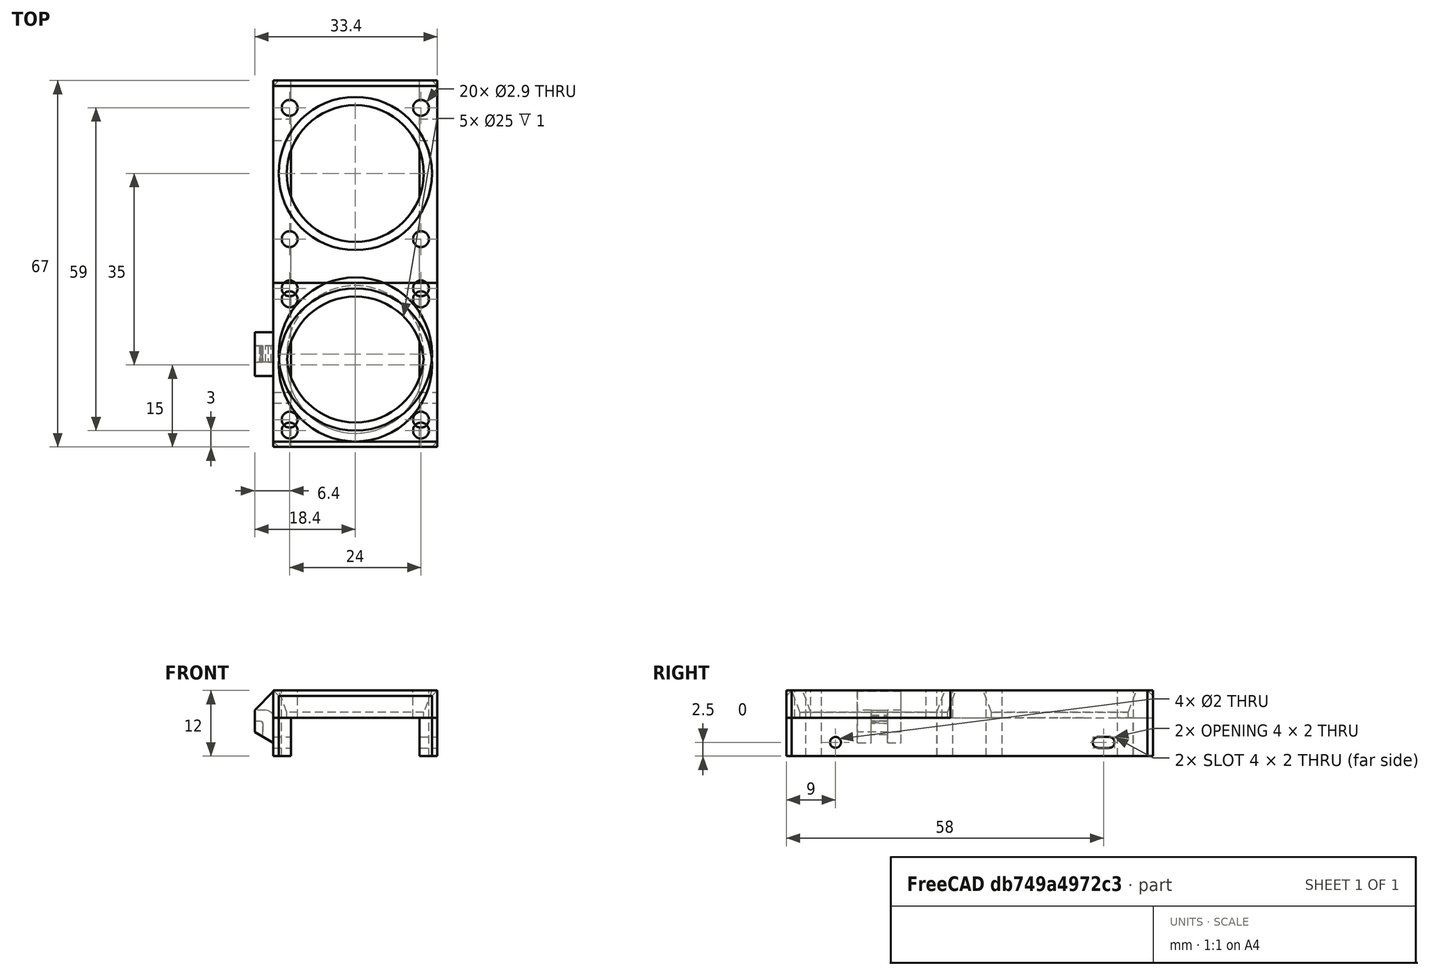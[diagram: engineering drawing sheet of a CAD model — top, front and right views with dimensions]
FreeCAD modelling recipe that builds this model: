
FCSTD DOCUMENT  (FreeCAD 0.18R16146 (Git))
Label: nvme-cooler-mount
License: All rights reserved
LicenseURL: http://en.wikipedia.org/wiki/All_rights_reserved
objects: Part::Cylinder×11, Part::Box×7, Part::MultiFuse×7, Part::Feature×6, Part::Cut×4, Part::Chamfer×2
note: 37 computed .brp shape members not serialized (recipe doc carries the construction recipe); baked Part::Feature solids carry a one-line shape summary decoded from their .brp

FEATURE [Part::Box] Box  label="Cube"
  AttacherType = Attacher::AttachEngine3D
  Height = 5
  Length = 30
  Placement = pos=(-15,-15,0) rot=(0,0,1;0rad)
  Width = 30
FEATURE [Part::Cylinder] Cylinder
  Angle = 360
  AttacherType = Attacher::AttachEngine3D
  Height = 10
  Placement = pos=(12,12,0) rot=(0,0,1;0rad)
  Radius = 1.45
FEATURE [Part::Cylinder] Cylinder001
  Angle = 360
  AttacherType = Attacher::AttachEngine3D
  Height = 10
  Placement = pos=(-12,12,0) rot=(0,0,1;0rad)
  Radius = 1.45
FEATURE [Part::Cylinder] Cylinder002
  Angle = 360
  AttacherType = Attacher::AttachEngine3D
  Height = 10
  Placement = pos=(12,-12,0) rot=(0,0,1;0rad)
  Radius = 1.45
FEATURE [Part::Cylinder] Cylinder003
  Angle = 360
  AttacherType = Attacher::AttachEngine3D
  Height = 10
  Placement = pos=(-12,-12,0) rot=(0,0,1;0rad)
  Radius = 1.45
FEATURE [Part::Cylinder] Cylinder004
  Angle = 360
  AttacherType = Attacher::AttachEngine3D
  Height = 10
  Radius = 12.5
FEATURE [Part::MultiFuse] Fusion
  Shapes = -> [Cylinder003,Cylinder001,Cylinder,Cylinder002]
FEATURE [Part::Cut] Cut
  Base = -> Box
  Tool = -> Fusion
FEATURE [Part::Cut] Cut001
  Base = -> Cut
  Tool = -> Cylinder004
FEATURE [Part::Chamfer] Chamfer  label="fan-template"
  Base = -> Cut001
  Edges = 1 edges: [Edge11 r1=1.5 r2=4]
FEATURE [Part::Feature] Chamfer001  label="fan-template001"
  Placement = pos=(0,2,0) rot=(0,0,1;0rad)
  shape: bbox 30 x 30 x 5 mm, 12 faces (baked)
FEATURE [Part::Feature] Chamfer002  label="fan-template002"
  Placement = pos=(0,35,0) rot=(0,0,1;0rad)
  shape: bbox 30 x 30 x 5 mm, 12 faces (baked)
FEATURE [Part::Box] Box001  label="Cube001"
  AttacherType = Attacher::AttachEngine3D
  Height = 5
  Length = 30
  Placement = pos=(-15,17,0) rot=(0,0,1;0rad)
  Width = 3
FEATURE [Part::Box] Box002  label="Cube002"
  AttacherType = Attacher::AttachEngine3D
  Height = 5
  Length = 30
  Placement = pos=(-15,-15,0) rot=(0,0,1;0rad)
  Width = 2
FEATURE [Part::Box] Box003  label="Cube003"
  AttacherType = Attacher::AttachEngine3D
  Height = 7
  Length = 3.25
  Placement = pos=(-15,-15,-7) rot=(0,0,1;0rad)
  Width = 67
FEATURE [Part::Box] Box004  label="Cube004"
  AttacherType = Attacher::AttachEngine3D
  Height = 7
  Length = 3.25
  Placement = pos=(11.75,-15,-7) rot=(0,0,1;0rad)
  Width = 67
FEATURE [Part::Box] Box005  label="Cube005"
  AttacherType = Attacher::AttachEngine3D
  Height = 5
  Length = 30
  Placement = pos=(-15,50,0) rot=(0,0,1;0rad)
  Width = 2
FEATURE [Part::Feature] Part__Feature001  label="Common003"
  Placement = pos=(-77.65,-16.5,25.4) rot=(0.707107,0.707107,0;3.14159rad)
  shape: bbox 3.5 x 8 x 9.5 mm, 30 faces (baked)
FEATURE [Part::Cylinder] Cylinder006
  Angle = 360
  AttacherType = Attacher::AttachEngine3D
  Height = 30
  Placement = pos=(-15,34,-4.5) rot=(0,1,0;1.5708rad)
  Radius = 1
FEATURE [Part::Cylinder] Cylinder007
  Angle = 360
  AttacherType = Attacher::AttachEngine3D
  Height = 30
  Placement = pos=(-15,33,-4.5) rot=(0,1,0;1.5708rad)
  Radius = 1
FEATURE [Part::Box] Box006  label="Cube006"
  AttacherType = Attacher::AttachEngine3D
  Height = 2
  Length = 30
  Placement = pos=(-15,33,-5.5) rot=(0,0,1;0rad)
  Width = 1
FEATURE [Part::MultiFuse] Fusion002
  Shapes = -> [Box003,Box004]
FEATURE [Part::Cylinder] Cylinder008
  Angle = 360
  AttacherType = Attacher::AttachEngine3D
  Height = 20
  Placement = pos=(-12,12,0) rot=(0,0,1;0rad)
  Radius = 1.45
FEATURE [Part::Cylinder] Cylinder009
  Angle = 360
  AttacherType = Attacher::AttachEngine3D
  Height = 20
  Placement = pos=(12,12,0) rot=(0,0,1;0rad)
  Radius = 1.45
FEATURE [Part::Cylinder] Cylinder010
  Angle = 360
  AttacherType = Attacher::AttachEngine3D
  Height = 20
  Placement = pos=(-12,-12,0) rot=(0,0,1;0rad)
  Radius = 1.45
FEATURE [Part::Cylinder] Cylinder011
  Angle = 360
  AttacherType = Attacher::AttachEngine3D
  Height = 20
  Placement = pos=(12,-12,0) rot=(0,0,1;0rad)
  Radius = 1.45
FEATURE [Part::MultiFuse] Fusion003002
  Placement = pos=(0,2,-11) rot=(0,0,1;0rad)
  Shapes = -> [Cylinder011,Cylinder010,Cylinder009,Cylinder008]
FEATURE [Part::Feature] Fusion003002001  label="Fusion003003"
  Placement = pos=(0,35,-11) rot=(0,0,1;0rad)
  shape: bbox 26.9 x 26.9 x 20 mm, 12 faces, 4 solids (baked)
FEATURE [Part::MultiFuse] Fusion003002002
  Placement = pos=(0,10,0) rot=(0,0,1;0rad)
  Shapes = -> [Cylinder006,Box006,Cylinder007]
FEATURE [Part::Feature] Fusion001001  label="Fusion003004"
  shape: bbox 30 x 51 x 2 mm, 9 faces, 2 solids (baked)
FEATURE [Part::MultiFuse] Fusion003002003
  Shapes = -> [Fusion003002002,Fusion001001]
FEATURE [Part::Cut] Cut002
  Base = -> Fusion002
  Tool = -> Fusion003002003
FEATURE [Part::MultiFuse] Fusion003002004
  Shapes = -> [Cut002,Box001,Box002,Chamfer001,Chamfer002,Box005,Part__Feature001]
FEATURE [Part::MultiFuse] Fusion003002005
  Shapes = -> [Fusion003002001,Fusion003002]
FEATURE [Part::Cut] Cut003
  Base = -> Fusion003002004
  Tool = -> Fusion003002005
FEATURE [Part::Feature] Cut003001  label="Cut004"
  shape: bbox 33.4 x 67 x 12 mm, 73 faces (baked)
FEATURE [Part::Chamfer] Chamfer003
  Base = -> Cut003001
  Edges = 6 edges r=1: [Edge111,Edge112,Edge185,Edge187,Edge196,Edge197]
